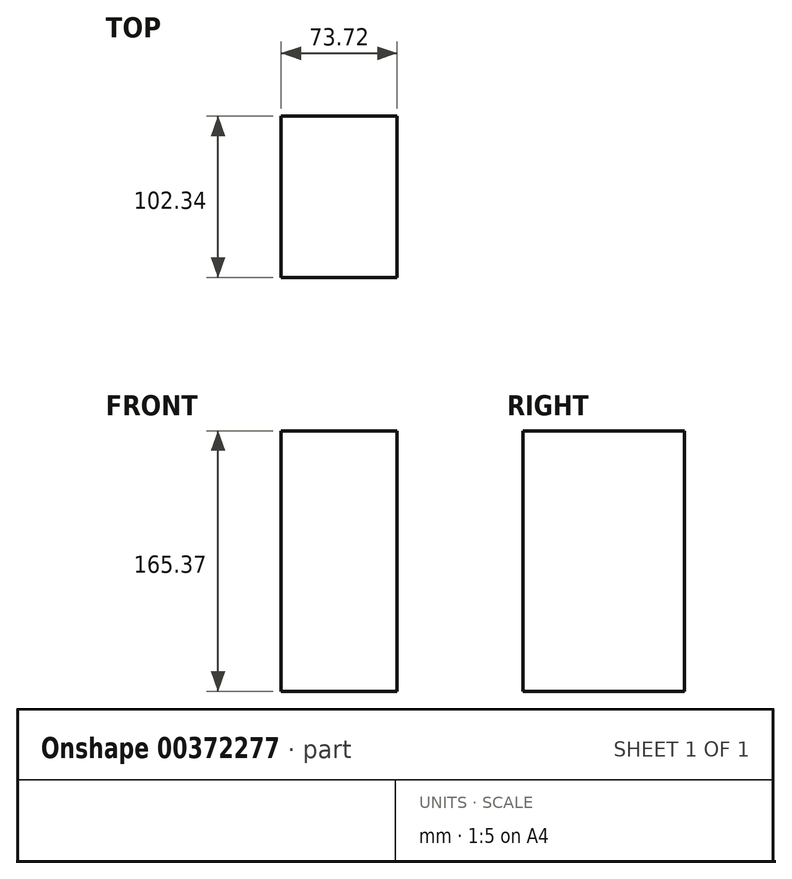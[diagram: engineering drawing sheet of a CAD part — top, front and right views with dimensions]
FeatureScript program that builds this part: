
annotation { "Feature Type Name" : "Feature", "Feature Type Description" : "" }
export const myFeature = defineFeature(function(context is Context, id is Id, definition is map)
    precondition{}
    {
        {
            var Q0;
            Q0=qCreatedBy(makeId("Right.planeOp"),FACE);
            var sketch = newSketch(context, id + "F0", { "sketchPlane" : qUnion([Q0])});
            skLineSegment(sketch, "E0.bottom", {"start": v(62.53, 124.34) * mm, "end": v(164.87, 124.34) * mm});
            skLineSegment(sketch, "E0.top", {"start": v(62.53, 289.7) * mm, "end": v(164.87, 289.7) * mm});
            skLineSegment(sketch, "E0.left", {"start": v(62.53, 124.34) * mm, "end": v(62.53, 289.7) * mm});
            skLineSegment(sketch, "E0.right", {"start": v(164.87, 124.34) * mm, "end": v(164.87, 289.7) * mm});
            skSolve(sketch);
        }
        {
            var Q0;
            Q0=makeQuery(id+"F0.imprint","IMPRINT",FACE,{"disambiguationData":[TD([[makeQuery(id+"F0.imprint","IMPRINT",EDGE,{"derivedFrom":sQuery(id+"F0.wireOp",EDGE,"E0.bottom")}),1.0]])]});
            extrude(context, id + "F1", {"entities" : qUnion([Q0]), "depth" : 73.72 * mm});
        }
    });
